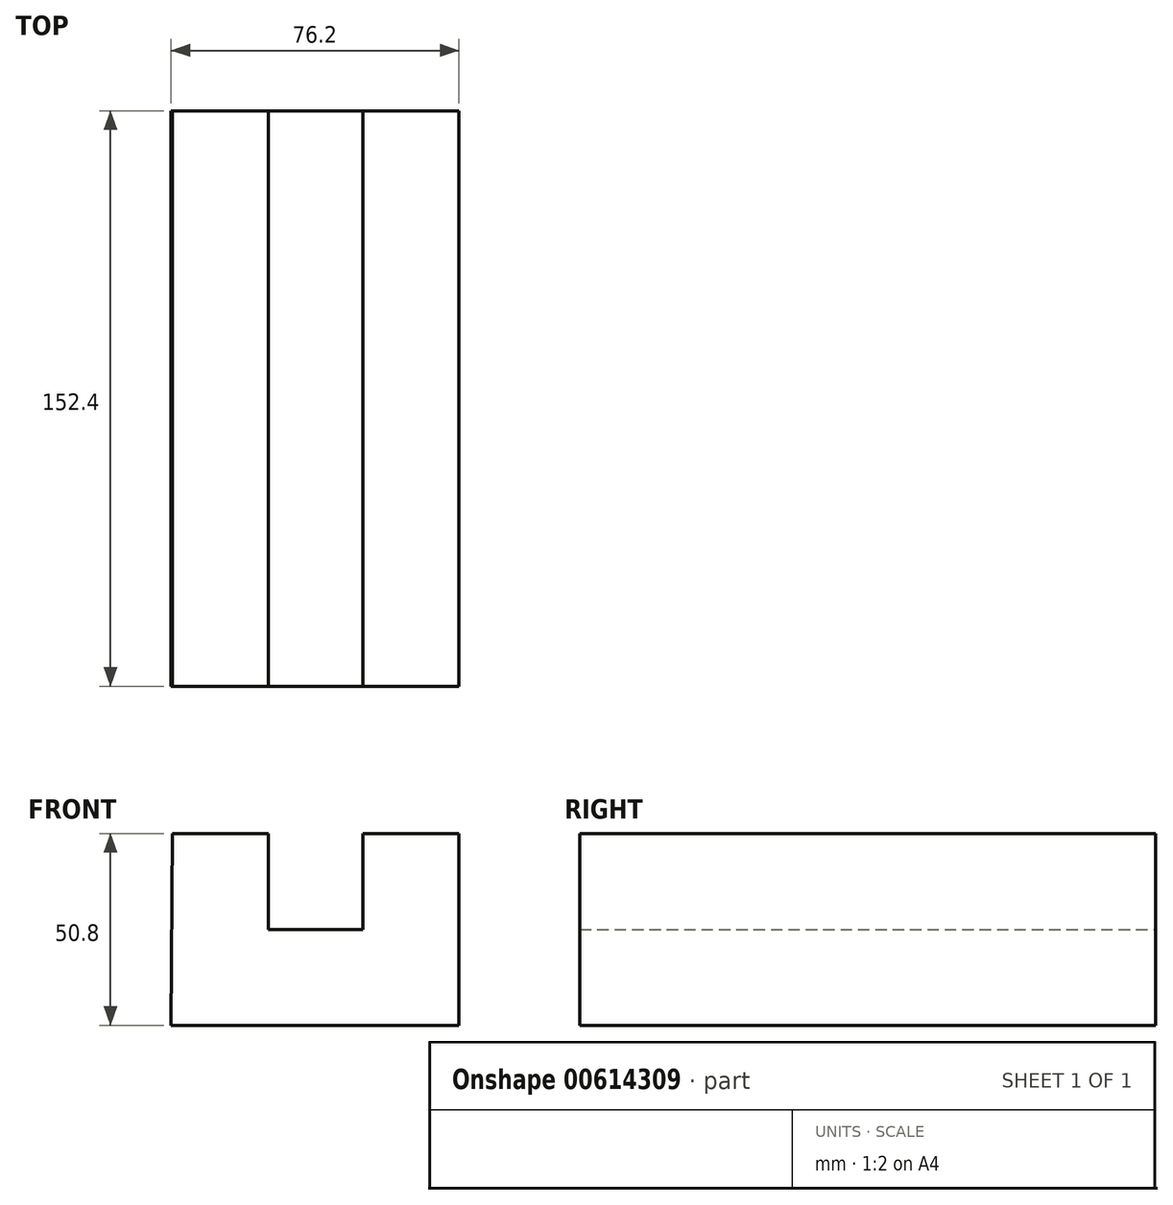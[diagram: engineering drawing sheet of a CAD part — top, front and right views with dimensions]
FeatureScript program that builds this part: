
annotation { "Feature Type Name" : "Feature", "Feature Type Description" : "" }
export const myFeature = defineFeature(function(context is Context, id is Id, definition is map)
    precondition{}
    {
        {
            var Q0;
            Q0=qCreatedBy(makeId("Front.planeOp"),FACE);
            var sketch = newSketch(context, id + "F0", { "sketchPlane" : qUnion([Q0])});
            skLineSegment(sketch, "E0", {"start": v(-76.2, 0) * mm, "end": v(0, 0) * mm});
            skLineSegment(sketch, "E1", {"start": v(0, 0) * mm, "end": v(0, 50.8) * mm});
            skLineSegment(sketch, "E2", {"start": v(0, 50.8) * mm, "end": v(-25.4, 50.8) * mm});
            skLineSegment(sketch, "E3", {"start": v(-25.4, 50.8) * mm, "end": v(-25.4, 25.4) * mm});
            skLineSegment(sketch, "E4", {"start": v(-25.4, 25.4) * mm, "end": v(-50.42, 25.4) * mm});
            skLineSegment(sketch, "E5", {"start": v(-50.42, 25.4) * mm, "end": v(-50.42, 50.8) * mm});
            skLineSegment(sketch, "E6", {"start": v(-50.42, 50.8) * mm, "end": v(-75.82, 50.8) * mm});
            skLineSegment(sketch, "E7", {"start": v(-75.82, 50.8) * mm, "end": v(-76.2, 0) * mm});
            skSolve(sketch);
        }
        {
            var Q0;
            Q0=makeQuery(id+"F0.imprint","IMPRINT",FACE,{"disambiguationData":[TD([[makeQuery(id+"F0.imprint","IMPRINT",EDGE,{"derivedFrom":sQuery(id+"F0.wireOp",EDGE,"E0")}),1.0]])]});
            extrude(context, id + "F1", {"entities" : qUnion([Q0]), "depth" : 152.4 * mm, "offsetDistance" : 25.4 * mm});
        }
    });
